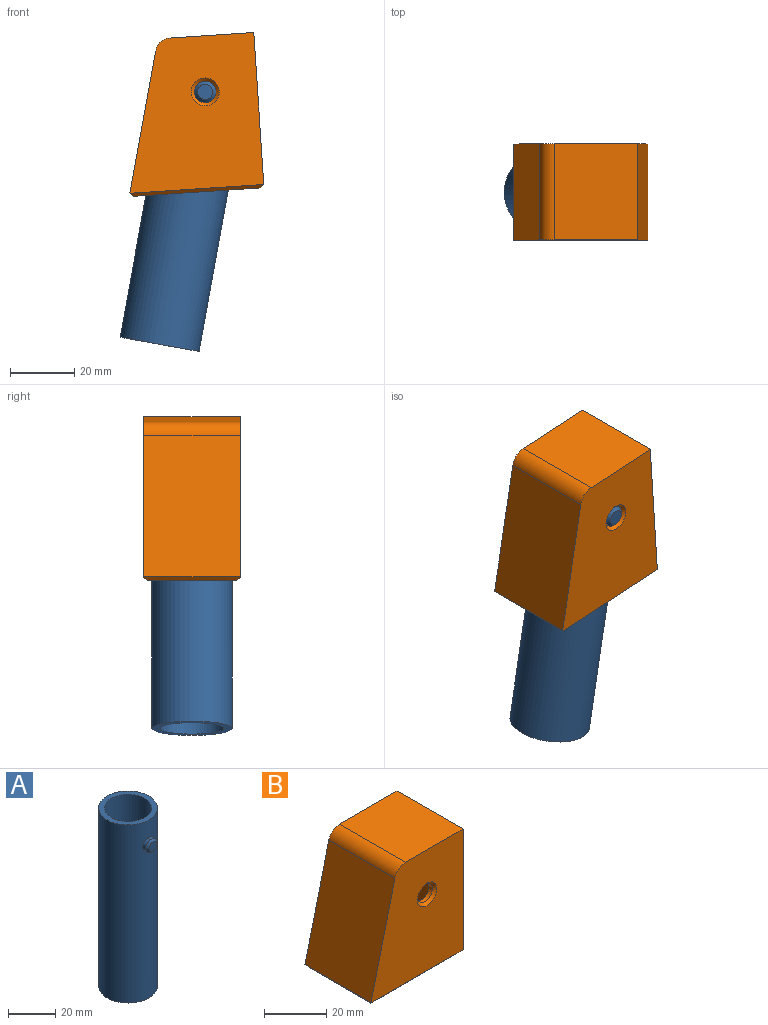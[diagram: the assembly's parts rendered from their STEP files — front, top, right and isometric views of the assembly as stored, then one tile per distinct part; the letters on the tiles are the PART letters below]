
ASSEMBLY  parts=2 mates=1
PART A: 14 faces, bbox 25x30x92.5 mm
  f0: cylinder r=3.38mm len=6.76mm, axis (0,1,0), area 36.8mm2, adj f2,f12
  f1: plane 4.76x4.76mm, normal (0,-1,0), area 17.8mm2, adj f12
  f2: cylinder r=12.5mm len=92.5mm, axis (0,0,-1), area 7192.6mm2, adj f0,f3,f4,f6
  f3: plane 25x25mm, normal (0,0,1), area 176.7mm2, adj f2,f9
  f4: plane 25x25mm, normal (0,0,-1), area 176.7mm2, adj f2,f9
  f5: plane 4.76x4.76mm, normal (0,1,0), area 17.8mm2, adj f13
  f6: cylinder r=3.38mm len=6.76mm, axis (0,1,0), area 36.7mm2, adj f2,f13
  f7: cylinder r=0.88mm len=2.54mm, axis (0,1,0), area 13.9mm2, adj f8,f9
  f8: plane 1.76x1.76mm, normal (0,1,0), area 2.4mm2, adj f7
  f9: cylinder r=10mm len=92.5mm, axis (0,0,-1), area 5807.1mm2, adj f3,f4,f7,f11
  f10: plane 1.76x1.76mm, normal (0,-1,0), area 2.4mm2, adj f11
  f11: cylinder r=0.88mm len=2.54mm, axis (0,1,0), area 13.9mm2, adj f9,f10
  f12: cone r=2.38mm half-angle=45deg, axis (0,1,0), area 25.6mm2, adj f0,f1
  f13: cone r=3.38mm half-angle=45deg, axis (0,-1,0), area 25.6mm2, adj f5,f6
PART B: 20 faces, bbox 41.8x30x48.5 mm
  f0: plane 39.85x28mm, normal (0,0,-1), area 189.5mm2, adj f6,f8,f9,f10,f16,f17,f18,f19
  f1: plane 47.51x30mm, normal (1,0,0), area 1425.2mm2, adj f2,f4,f5,f16
  f2: plane 30x26.1mm, normal (0,0,1), area 782.9mm2, adj f1,f4,f5,f13
  f3: plane 43.48x30mm, normal (-0.97,0,0.24), area 1344.5mm2, adj f4,f5,f13,f19
  f4: plane 47.51x41.82mm, normal (0,-1,0), area 1644.2mm2, adj f1,f2,f3,f13,f14,f17,f19
  f5: plane 47.51x41.82mm, normal (0,1,0), area 1644.2mm2, adj f1,f2,f3,f13,f15,f18,f19
  f6: plane 46.01x25mm, normal (-1,0,0), area 1150.2mm2, adj f0,f7,f9,f10
  f7: plane 25.55x25mm, normal (0,0,-1), area 638.7mm2, adj f6,f8,f9,f10
  f8: plane 46.01x25mm, normal (0.97,0,-0.24), area 1185.6mm2, adj f0,f7,f9,f10
  f9: plane 46.01x37.05mm, normal (0,1,0), area 1404.2mm2, adj f0,f6,f7,f8,f12
  f10: plane 46.01x37.05mm, normal (0,-1,0), area 1404.2mm2, adj f0,f6,f7,f8,f11
  f11: cylinder r=3.38mm len=6.76mm, axis (0,-1,0), area 31.8mm2, adj f10,f15
  f12: cylinder r=3.38mm len=6.76mm, axis (0,-1,0), area 31.8mm2, adj f9,f14
  f13: cylinder r=5mm len=30mm, axis (0,-1,0), area 198.9mm2, adj f2,f3,f4,f5
  f14: cone r=3.38mm half-angle=45deg, axis (0,-1,0), area 34.5mm2, adj f4,f12
  f15: cone r=3.38mm half-angle=45deg, axis (0,1,0), area 34.5mm2, adj f5,f11
  f16: plane 30x1mm, normal (0.71,0,-0.71), area 41mm2, adj f0,f1,f17,f18
  f17: plane 41.63x1mm, normal (0,-0.71,-0.71), area 57.6mm2, adj f0,f4,f16,f19
  f18: plane 41.63x1mm, normal (0,0.71,-0.71), area 57.6mm2, adj f0,f5,f16,f19
  f19: plane 30x1.24mm, normal (-0.79,0,-0.62), area 46mm2, adj f0,f3,f4,f5,f17,f18
PLACE A rot(axis=(0,1,0),10.2deg) t=(-93.3,-20.16,-35.73)mm
PLACE B rot(axis=(0,-1,0),3.8deg) t=(-91.37,-20.16,21.68)mm fixed
MATE revolute A.f0 <-> B.f11  axis (0,1,0) through (-79.08,-5.16,43)mm
